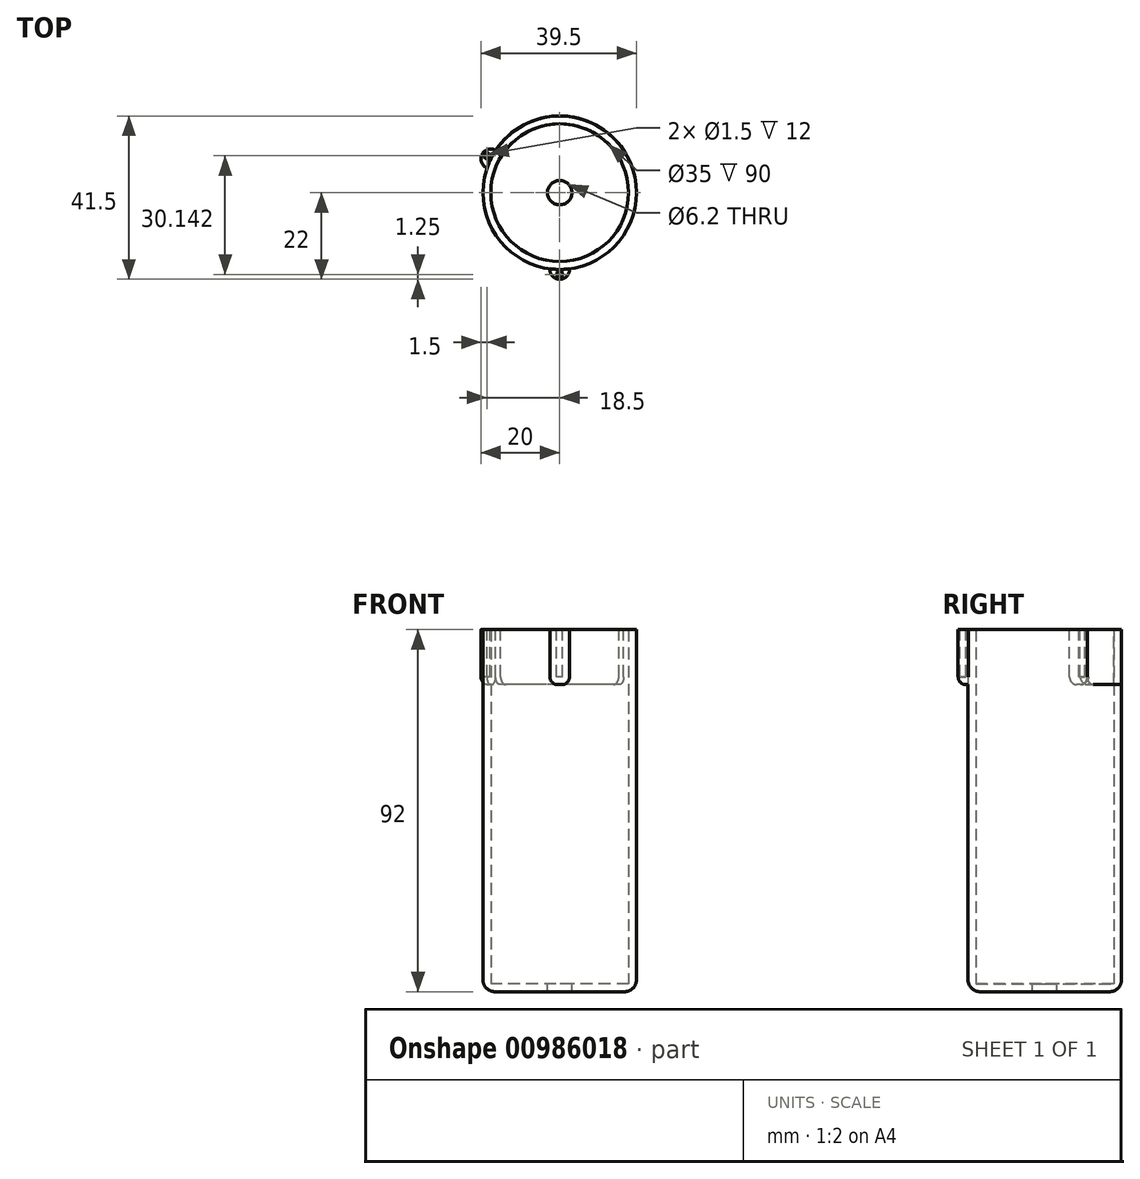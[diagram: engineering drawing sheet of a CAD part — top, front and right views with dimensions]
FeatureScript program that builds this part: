
annotation { "Feature Type Name" : "Feature", "Feature Type Description" : "" }
export const myFeature = defineFeature(function(context is Context, id is Id, definition is map)
    precondition{}
    {
        {
            var Q0;
            Q0=qCreatedBy(makeId("Top.planeOp"),FACE);
            var sketch = newSketch(context, id + "F0", { "sketchPlane" : qUnion([Q0])});
            skCircle(sketch, "E0", {"center": v(0, 0) * mm, "radius": 19.5 * mm});
            skSolve(sketch);
        }
        {
            var Q0;
            Q0 = qSketchRegion(id + "F0", true);
            extrude(context, id + "F1", {"entities" : qUnion([Q0]), "depth" : 92 * mm, "offsetDistance" : 25 * mm});
        }
        {
            var Q0;
            Q0=makeQuery(id+"F1.opExtrude","CAP_FACE",FACE,{"disambiguationData":[OSD([sQuery(id+"F0.wireOp",EDGE,"E0")])],"isStart":false});
            shell(context, id + "F2", {"entities" : qUnion([Q0]), "thickness" : 2 * mm});
        }
        {
            var Q0;
            Q0=makeQuery(id+"F1.opExtrude","CAP_FACE",FACE,{"disambiguationData":[OSD([sQuery(id+"F0.wireOp",EDGE,"E0")])],"isStart":false});
            var sketch = newSketch(context, id + "F3", { "sketchPlane" : qUnion([Q0])});
            skCircle(sketch, "E1", {"center": v(0, 0) * mm, "radius": 3.1 * mm});
            skSolve(sketch);
        }
        {
            var Q0;
            Q0 = qSketchRegion(id + "F3", true);
            extrude(context, id + "F4", {"entities" : qUnion([Q0]), "operationType" : NewBodyOperationType.REMOVE, "oppositeDirection" : true, "depth" : 93 * mm, "offsetDistance" : 25 * mm});
        }
        {
            var Q0;
            Q0=makeQuery(id+"F1.opExtrude","CAP_FACE",FACE,{"disambiguationData":[OSD([sQuery(id+"F0.wireOp",EDGE,"E0")])],"isStart":false});
            var sketch = newSketch(context, id + "F5", { "sketchPlane" : qUnion([Q0])});
            skCircle(sketch, "E2", {"center": v(-17.5, 8.6) * mm, "radius": 2.5 * mm});
            skCircle(sketch, "E3", {"center": v(0, -19.5) * mm, "radius": 2.5 * mm});
            skLineSegment(sketch, "E4", {"start": v(0, 17.5) * mm, "end": v(0, -17.5) * mm, "construction": true});
            skCircle(sketch, "E5.MirrorC", {"center": v(17.5, 8.6) * mm, "radius": 2.5 * mm});
            skLineSegment(sketch, "E6", {"start": v(-17.5, 8.6) * mm, "end": v(17.5, 8.6) * mm, "construction": true});
            skLineSegment(sketch, "E7", {"start": v(-19.5, 0) * mm, "end": v(19.5, 0) * mm, "construction": true});
            skSolve(sketch);
        }
        {
            var Q0;
            {var subQ0=sQuery(id+"F5.wireOp",EDGE,"E2");var subQ1=makeQuery(id+"F1.opExtrude","CAP_EDGE",EDGE,{"disambiguationData":[OSD([sQuery(id+"F0.wireOp",EDGE,"E0")])],"isStart":false});var subQ2=makeQuery(id+"F5.imprint","INTERSECT",VERTEX,{"disambiguationData":[OD(0.0)],"derivedFrom":[subQ1,subQ0]});Q0=makeQuery(id+"F5.imprint","IMPRINT",FACE,{"disambiguationData":[TD([[makeQuery(id+"F5.imprint","IMPRINT",EDGE,{"disambiguationData":[TD([[subQ2,-1.0]])],"derivedFrom":subQ0}),1.0]])]});}
            var Q1;
            {var subQ0=sQuery(id+"F5.wireOp",EDGE,"E3");var subQ1=makeQuery(id+"F1.opExtrude","CAP_EDGE",EDGE,{"disambiguationData":[OSD([sQuery(id+"F0.wireOp",EDGE,"E0")])],"isStart":false});var subQ2=makeQuery(id+"F5.imprint","INTERSECT",VERTEX,{"disambiguationData":[OD(0.0)],"derivedFrom":[subQ1,subQ0]});Q1=makeQuery(id+"F5.imprint","IMPRINT",FACE,{"disambiguationData":[TD([[makeQuery(id+"F5.imprint","IMPRINT",EDGE,{"disambiguationData":[TD([[subQ2,1.0]])],"derivedFrom":subQ0}),1.0]])]});}
            var Q2;
            {var subQ0=sQuery(id+"F5.wireOp",EDGE,"E5.MirrorC");var subQ1=makeQuery(id+"F1.opExtrude","CAP_EDGE",EDGE,{"disambiguationData":[OSD([sQuery(id+"F0.wireOp",EDGE,"E0")])],"isStart":false});var subQ2=makeQuery(id+"F5.imprint","INTERSECT",VERTEX,{"disambiguationData":[OD(0.0)],"derivedFrom":[subQ1,subQ0]});Q2=makeQuery(id+"F5.imprint","IMPRINT",FACE,{"disambiguationData":[TD([[makeQuery(id+"F5.imprint","IMPRINT",EDGE,{"disambiguationData":[TD([[subQ2,-1.0]])],"derivedFrom":subQ0}),-1.0]])]});}
            extrude(context, id + "F6", {"entities" : qUnion([Q0, Q1, Q2]), "oppositeDirection" : true, "depth" : 14 * mm, "offsetDistance" : 25 * mm});
        }
        {
            var Q0;
            Q0=makeQuery(id+"F1.opExtrude","CAP_FACE",FACE,{"disambiguationData":[OSD([sQuery(id+"F0.wireOp",EDGE,"E0")])],"isStart":false});
            var sketch = newSketch(context, id + "F7", { "sketchPlane" : qUnion([Q0])});
            skLineSegment(sketch, "E8", {"start": v(-16.16, 10.92) * mm, "end": v(-17.42, 8.76) * mm, "construction": true});
            skLineSegment(sketch, "E9", {"start": v(0, 17.5) * mm, "end": v(0, -19.5) * mm, "construction": true});
            skLineSegment(sketch, "E10", {"start": v(-17.42, 8.76) * mm, "end": v(-18.5, 9.4) * mm, "construction": true});
            skCircle(sketch, "E11", {"center": v(-18.5, 9.4) * mm, "radius": 0.75 * mm});
            skCircle(sketch, "E12.MirrorC", {"center": v(18.5, 9.4) * mm, "radius": 0.75 * mm});
            skLineSegment(sketch, "E13", {"start": v(0, -19.5) * mm, "end": v(0, -20.75) * mm, "construction": true});
            skCircle(sketch, "E14", {"center": v(0, -20.75) * mm, "radius": 0.75 * mm});
            skLineSegment(sketch, "E15", {"start": v(-18.5, 9.4) * mm, "end": v(18.5, 9.4) * mm, "construction": true});
            skSolve(sketch);
        }
        {
            var Q0;
            Q0=makeQuery(id+"F7.imprint","IMPRINT",FACE,{"disambiguationData":[TD([[makeQuery(id+"F7.imprint","IMPRINT",EDGE,{"derivedFrom":sQuery(id+"F7.wireOp",EDGE,"E12.MirrorC")}),-1.0]])]});
            var Q1;
            Q1=makeQuery(id+"F7.imprint","IMPRINT",FACE,{"disambiguationData":[TD([[makeQuery(id+"F7.imprint","IMPRINT",EDGE,{"derivedFrom":sQuery(id+"F7.wireOp",EDGE,"E14")}),1.0]])]});
            extrude(context, id + "F8", {"entities" : qUnion([Q0, Q1]), "operationType" : NewBodyOperationType.REMOVE, "oppositeDirection" : true, "depth" : 12 * mm, "offsetDistance" : 25 * mm});
        }
        {
            var Q0;
            Q0=sQuery(id+"F7.wireOp",EDGE,"E11");
            extrude(context, id + "F9", {"bodyType" : ToolBodyType.SURFACE, "surfaceEntities" : qUnion([Q0]), "oppositeDirection" : true, "depth" : 12 * mm, "offsetDistance" : 25 * mm});
        }
        {
            var Q0;
            Q0 = qSketchRegion(id + "F7", true);
            extrude(context, id + "F10", {"entities" : qUnion([Q0]), "operationType" : NewBodyOperationType.REMOVE, "oppositeDirection" : true, "depth" : 12 * mm, "offsetDistance" : 25 * mm});
        }
        {
            var Q0;
            Q0=makeQuery(id+"F6.opExtrude","CAP_EDGE",EDGE,{"disambiguationData":[OSD([sQuery(id+"F5.wireOp",EDGE,"E2")])],"isStart":false});
            var Q1;
            Q1=makeQuery(id+"F6.opExtrude","CAP_EDGE",EDGE,{"disambiguationData":[OSD([sQuery(id+"F5.wireOp",EDGE,"E3")])],"isStart":false});
            var Q2;
            Q2=makeQuery(id+"F6.opExtrude","CAP_EDGE",EDGE,{"disambiguationData":[OSD([sQuery(id+"F5.wireOp",EDGE,"E5.MirrorC")])],"isStart":false});
            fillet(context, id + "F11", {"entities" : qUnion([Q0, Q1, Q2]), "radius" : 2 * mm, "tangentPropagation" : true, "allowEdgeOverflow" : false});
        }
        {
            var Q0;
            Q0=makeQuery(id+"F1.opExtrude","CAP_EDGE",EDGE,{"disambiguationData":[OSD([sQuery(id+"F0.wireOp",EDGE,"E0")])],"isStart":true});
            fillet(context, id + "F12", {"entities" : qUnion([Q0]), "radius" : 3 * mm, "tangentPropagation" : true, "allowEdgeOverflow" : false});
        }
    });
